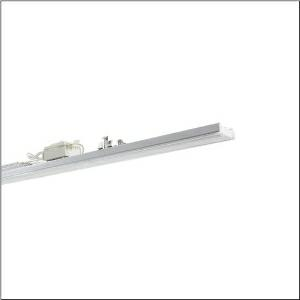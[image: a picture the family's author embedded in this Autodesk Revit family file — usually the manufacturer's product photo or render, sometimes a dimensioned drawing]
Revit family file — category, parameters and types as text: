
# Revit family: licross_21_recessed_ho_51te12vn4cxm
name_source: partatom
category: Lighting Fixtures
units: mm (PartAtom-declared; Revit-internal decimal feet)

## family parameters
Cut with Voids When Loaded = No
Host = Face
Light Source = No
Part Type = Normal
Room Calculation Point = No
Round Connector Dimension = Use Diameter
Shared = No

## types (1)
- --- (1 x LED, 12000 lm, 64.8 W, 4000K)
    Apparent Load = 65 VA
    CIE Flux Codes = 66 91 98 100 100
    Color Rendering = 80
    Color Temperature = 4000K
    Default Elevation = 1800 mm
    Description = Licross 21 Recessed HO, luminaire insert, of sheet steel, galvanised, coil coated, white, length: 1.500mm, width: 66mm, height: 67mm, LED rated luminous flux: 12.000lm, light colour: 840, SDCM (Standard Deviation of Colour Matching)MacAdam ≤ 2 SDCM (initial), control gear: DALI 2, CLO, with plug, 5-pole, with phase selection, mains connection: 220..240V, AC, 50/60Hz, start of lifetime: 65W, end of service life: 72W, internal wiring halogen-free, primary optical cover: cover, of PMMA, light emission: direct distribution, primary light characteristic: symmetric, protection rating (complete): IP54, insulation class (complete): insulation class I (protective earthing), certification: CE, ENEC, VDE, UKCA, protection symbol: D if used in an environment with non-conductive dust loads with corresponding accessories, impact resistance: IK06, permissible ambient temperature for indoor applications: -25..+30°C, corresponds to IFS (International Featured Standards) requirements for safety and quality in the food industry, reducing of maximum allowable ambient temperature of 5°C with ceiling mounting, LABS conformity tested according to VDMA 24364:2018-05, The light source and the operating device comply with the requirements of the Ecodesign Regulation (EU) 2019/2020 and are replaceable in accordance with this regulation, packaging unit: 1 piece
    Height = 58 mm
    Lamp = 1 x LED
    Lamp Light Flux = 12000 lm
    Lamp Power = 64.8 W
    Lamp count = 1
    Length = 1500 mm
    Luminous efficacy = 185 lm/W
    Manufacturer = Siteco
    ModVariant = No
    Model = 51TE12VN4CXM
    Mounting Place = Ceiling
    Mounting Type = Pendant
    Number of Poles = 1
    OnlyDefault = Yes
    Power Factor = 1
    Product Name = Licross 21 Recessed HO
    Product group = luminaire insert | ceiling pendant
    ProductGroupID = 901
    Protection Class = Protection class I
    Protection Degree = IP 54
    RLX_Detail_Level = 1
    RLX_Emergency_Light_Flux = 0 lm
    RLX_Emergency_Type = 0
    RLX_Emergency_Type_DB = No
    RlxData = <blob elided: 24833 chars, md5=0a6b082b>
    Socket = socket
    Standby Power = 0 W
    System Light Flux = 12000 lm
    System Power = 65 W
    Type Comments = factory setting: luminous flux: 100 % | dim-lin: 254 | 441 mA
    Type Image = l_1296930.jpg
    URL = http://relux.com
    VarID = @adj_092563
    Voltage = 0 V
    Weight = 0.00 kg
    Width = 66 mm

## geometry (parser evidence)
native form markers: Blend x4, Sweep x11
no freeform markers — native parametric forms only
